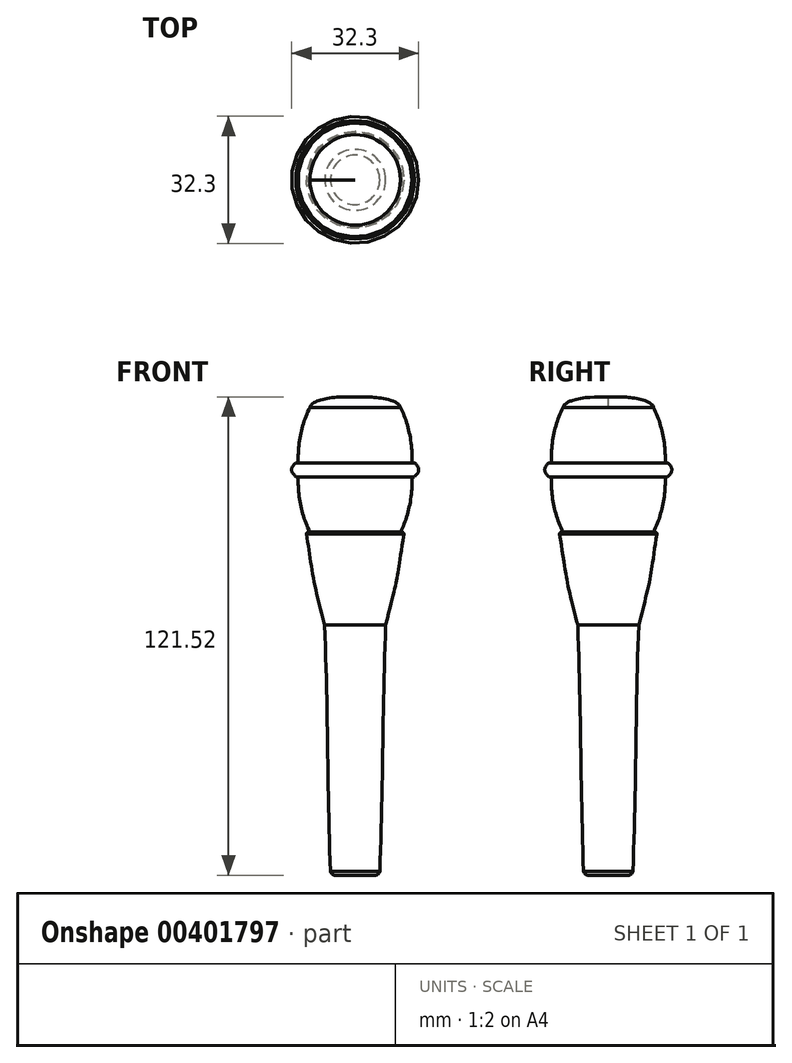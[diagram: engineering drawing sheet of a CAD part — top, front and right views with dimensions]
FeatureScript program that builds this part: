
annotation { "Feature Type Name" : "Feature", "Feature Type Description" : "" }
export const myFeature = defineFeature(function(context is Context, id is Id, definition is map)
    precondition{}
    {
        {
            var Q0;
            Q0=qCreatedBy(makeId("Front.planeOp"),FACE);
            var sketch = newSketch(context, id + "F0", { "sketchPlane" : qUnion([Q0])});
            skFitSpline(sketch, "E0", {"points": [v(-7.74, 3.5) * mm, v(-6.27, -59.18) * mm], "startDerivative": vector(2.4, -62.5) * mm, "endDerivative": vector(2.4, -62.5) * mm});
            skFitSpline(sketch, "E1", {"points": [v(-7.74, 3.5) * mm, v(-12.35, 26.55) * mm], "startDerivative": vector(-9.96, 38.16) * mm, "endDerivative": vector(-5.71, 37.24) * mm});
            skLineSegment(sketch, "E2", {"start": v(-11.95, 27.1) * mm, "end": v(-11.5, 27.1) * mm});
            skArc(sketch, "E3", {"start": v(-12.35, 26.55) * mm, "mid": v(-12.26, 26.9) * mm, "end": v(-11.95, 27.1) * mm});
            skLineSegment(sketch, "E4", {"start": v(-14.44, 41.13) * mm, "end": v(-15.05, 41.13) * mm});
            skFitSpline(sketch, "E5", {"points": [v(-14.44, 41.13) * mm, v(-11.5, 27.1) * mm], "startDerivative": vector(-0.82, -13.65) * mm, "endDerivative": vector(5.88, -10.92) * mm});
            skLineSegment(sketch, "E6", {"start": v(-5.11, -60.1) * mm, "end": v(0, -60.1) * mm});
            skArc(sketch, "E7", {"start": v(-5.11, -60.1) * mm, "mid": v(-5.85, -59.84) * mm, "end": v(-6.27, -59.18) * mm});
            skLineSegment(sketch, "E8.MirrorCS", {"start": v(-14.44, 44.7) * mm, "end": v(-15.05, 44.7) * mm});
            skFitSpline(sketch, "E9", {"points": [v(-15.05, 44.7) * mm, v(-15.05, 41.13) * mm], "startDerivative": vector(-5.14, -4.2) * mm, "endDerivative": vector(3.58, -3.13) * mm});
            skFitSpline(sketch, "E10.MirrorCS", {"points": [v(-14.44, 44.7) * mm, v(-11.5, 58.74) * mm], "startDerivative": vector(-0.82, 13.65) * mm, "endDerivative": vector(5.88, 10.92) * mm});
            skFitSpline(sketch, "E11", {"points": [v(-11.5, 58.74) * mm, v(0, 61.34) * mm], "startDerivative": vector(1.13, 6.42) * mm, "endDerivative": vector(14.26, -1.1) * mm});
            skLineSegment(sketch, "E12", {"start": v(0, 61.34) * mm, "end": v(0, -60.1) * mm});
            skSolve(sketch);
        }
        {
            var Q0;
            Q0 = qSketchRegion(id + "F0", true);
            var Q1;
            Q1=sQuery(id+"F0.wireOp",EDGE,"E12");
            revolve(context, id + "F1", {"entities" : qUnion([Q0]), "axis" : qUnion([Q1]), "revolveType" : RevolveType.FULL});
        }
    });
